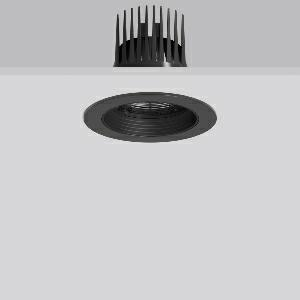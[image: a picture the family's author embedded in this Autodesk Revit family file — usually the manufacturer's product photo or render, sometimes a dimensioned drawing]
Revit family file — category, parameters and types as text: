
# Revit family: heledon_maxi_e_901767_003_0ec3
name_source: partatom
category: Lighting Fixtures
units: mm (PartAtom-declared; Revit-internal decimal feet)

## family parameters
Cut with Voids When Loaded = No
Host = Face
Light Source = No
Part Type = Normal
Room Calculation Point = No
Round Connector Dimension = Use Diameter
Shared = No

## types (1)
- HELEDON maxi E (1 x LED Modul 930, 3650 lm, 3000)
    Apparent Load = 35 VA
    Approval mark = CE
    CIE Flux Codes = 97 100 100 100 100
    Color Rendering = 90
    Color Temperature = 3000
    Default Elevation = 1800 mm
    Description = Series: HELEDON maxi
Round recessed downlight. Housing: die-cast aluminium, powder-coated. Black plastic ring and recessed LED to prevent glare from the side. Optical assembly with lens made of plastic (polycarbonate) for the best homogeneous light distribution - can be changed without tools. Best colour rendering index Ra>90. Suitable for Recessed ceiling mounting. Installation without tools thanks to spring fastening system. Including separate LED converter with connecting cable 600 mm.High quality converter without flickering and stroboscopic effect. Through-wiring box (5 pole) available as accessory. The following accessories can be mounted without use of tools: interchangeable lenses, decorative glasses, honeycomb louvre, clear and frosted diffusers, white interchangeable plastic ring. 
Colour: deep black, matt (RAL 9005)
Diameter: 162 mm
Height: 3 mm
Cut-out diameter: 152 mm
Recess height: 200 mm
Luminaire: recess height: 135 mm
Lamp: LED
Socket: without socket
Colour temperature: 3000K
Colour rendering index (CRI): 92
System power: 35 W
Rated luminous flux: 3650 lm
Luminous efficiency: 104 lm/W
Control gear: Regulated power supply
Protection class: II
Type of protection: IP 20
    Height = 0 mm  [stored 0 ft]
    Lamp = 1 x LED Modul 930
    Lamp Light Flux = 3650 lm
    Lamp count = 1
    Length = 162 mm
    Lifetime = 50000 h
    Luminous efficacy = 104 lm/W
    Manufacturer = RZB
    ModVariant = No
    Model = 901767.003
    Mounting Place = Ceiling
    Mounting Type = Recessed
    Number of Poles = 1
    OnlyDefault = Yes
    Power Factor = 1
    Product Name = HELEDON maxi E
    Product group = Recessed downlights
    ProductGroupID = 402
    Protection Class = Protection class II
    Protection Degree = IP 20
    RLX_Detail_Level = 1
    RLX_Emergency_Light_Flux = 0 lm
    RLX_Emergency_Type = 0
    RLX_Emergency_Type_DB = No
    RlxData = <blob elided: 121237 chars, md5=45aaf961>
    Socket = socket
    Standby Power = 0 W
    System Light Flux = 3650 lm
    System Power = 35 W
    Type Comments = Product without accessories
    Type Image = 901663.003.jpg
    URL = http://relux.com
    VarID = ---
    Voltage = 230 V
    Voltage Range = 220-240 V
    Weight = 0.00 kg
    Width = 0 mm  [stored 0 ft]

note: [stored X ft] marks values corroborated as IEEE doubles in the binary element streams (Revit-internal decimal feet)

## geometry (parser evidence)
native form markers: Blend x4, Sweep x13
no freeform markers — native parametric forms only
